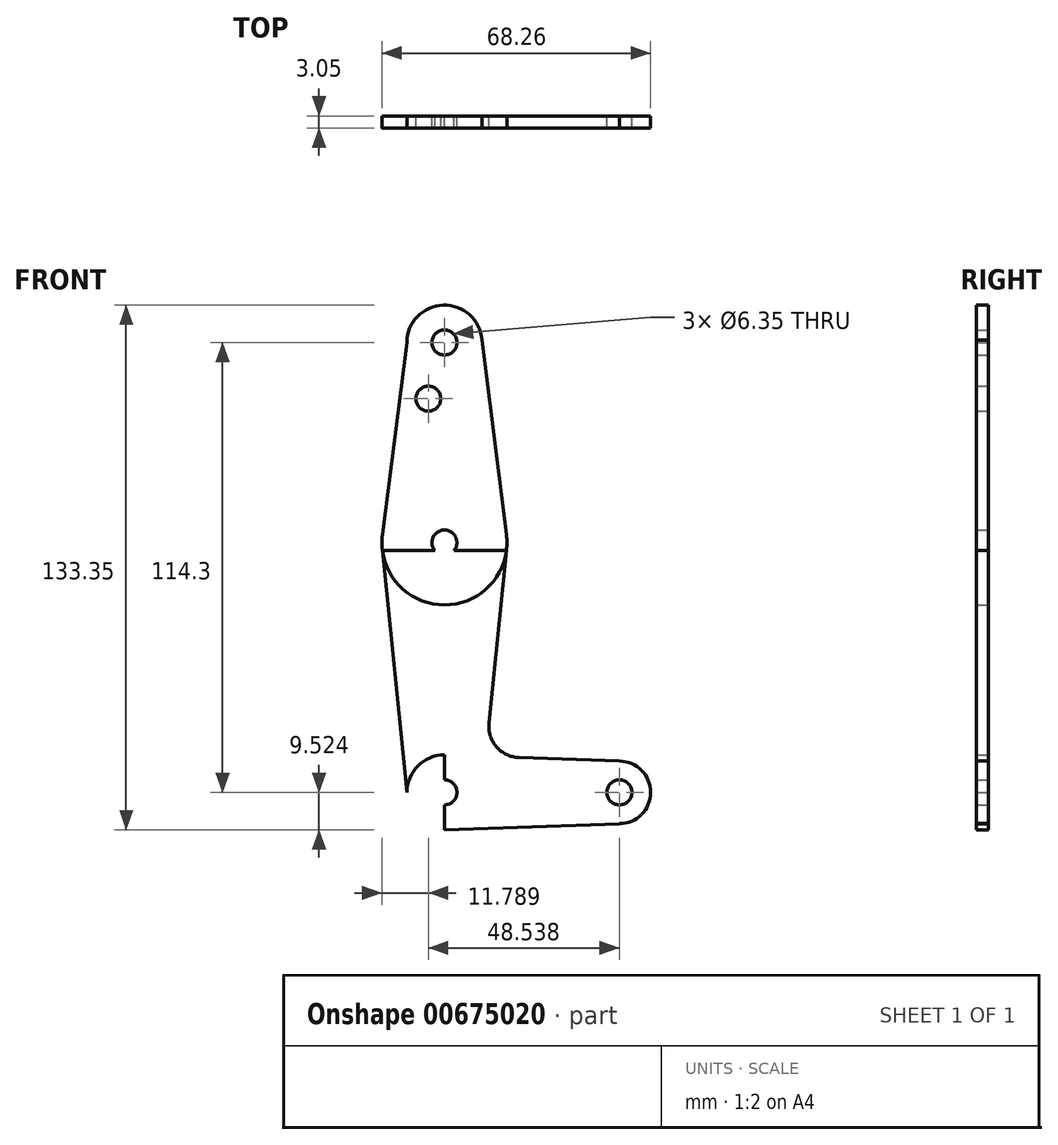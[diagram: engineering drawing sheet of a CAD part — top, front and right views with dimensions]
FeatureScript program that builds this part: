
annotation { "Feature Type Name" : "Feature", "Feature Type Description" : "" }
export const myFeature = defineFeature(function(context is Context, id is Id, definition is map)
    precondition{}
    {
        {
            var Q0;
            Q0=qCreatedBy(makeId("Front.planeOp"),FACE);
            var sketch = newSketch(context, id + "F0", { "sketchPlane" : qUnion([Q0])});
            skLineSegment(sketch, "E0", {"start": v(-73.87, 63.95) * mm, "end": v(-73.87, -50.35) * mm});
            skLineSegment(sketch, "E1", {"start": v(-73.87, -50.35) * mm, "end": v(-29.42, -50.35) * mm});
            skCircle(sketch, "E2", {"center": v(-29.42, -50.35) * mm, "radius": 7.94 * mm});
            skCircle(sketch, "E3", {"center": v(-73.87, 13.15) * mm, "radius": 15.88 * mm});
            skCircle(sketch, "E4", {"center": v(-73.87, 63.95) * mm, "radius": 9.53 * mm});
            skLineSegment(sketch, "E5", {"start": v(-73.87, -50.35) * mm, "end": v(-73.87, 13.15) * mm});
            skCircle(sketch, "E6", {"center": v(-73.87, -50.35) * mm, "radius": 9.53 * mm});
            skLineSegment(sketch, "E7", {"start": v(-64.37, 64.59) * mm, "end": v(-58.12, 15.14) * mm});
            skLineSegment(sketch, "E8", {"start": v(-62.57, -32.75) * mm, "end": v(-58.12, 11.12) * mm});
            skLineSegment(sketch, "E9", {"start": v(-83.4, 63.95) * mm, "end": v(-89.62, 15.14) * mm});
            skLineSegment(sketch, "E10", {"start": v(-83.4, -50.35) * mm, "end": v(-89.62, 11.12) * mm});
            skLineSegment(sketch, "E11", {"start": v(-29.42, -42.4) * mm, "end": v(-54.94, -41.5) * mm});
            skLineSegment(sketch, "E12", {"start": v(-73.87, -59.87) * mm, "end": v(-29.42, -58.29) * mm});
            skCircle(sketch, "E13", {"center": v(-73.87, 63.95) * mm, "radius": 3.18 * mm});
            skCircle(sketch, "E14", {"center": v(-73.87, 13.15) * mm, "radius": 3.18 * mm});
            skCircle(sketch, "E15", {"center": v(-73.87, -50.35) * mm, "radius": 3.18 * mm});
            skCircle(sketch, "E16", {"center": v(-29.42, -50.35) * mm, "radius": 3.18 * mm});
            skPoint(sketch, "E17.newPointB", {"position": v(-73.87, -40.81) * mm});
            skArc(sketch, "E17.filletArc", {"start": v(-62.57, -32.75) * mm, "mid": v(-60.65, -38.77) * mm, "end": v(-54.94, -41.5) * mm});
            skLineSegment(sketch, "E18", {"start": v(-73.87, 49.68) * mm, "end": v(-73.87, 13.15) * mm, "construction": true});
            skCircle(sketch, "E19", {"center": v(-77.96, 49.68) * mm, "radius": 3.18 * mm});
            skLineSegment(sketch, "E20", {"start": v(-89.62, 11.12) * mm, "end": v(-58.12, 11.12) * mm});
            skLineSegment(sketch, "E21", {"start": v(-73.87, -59.87) * mm, "end": v(-73.87, -50.35) * mm});
            skLineSegment(sketch, "E22", {"start": v(-29.42, -42.4) * mm, "end": v(-29.42, -58.29) * mm});
            skSolve(sketch);
        }
        {
            var Q0;
            {var subQ0=sQuery(id+"F0.wireOp",EDGE,"E9");Q0=makeQuery(id+"F0.imprint","IMPRINT",FACE,{"disambiguationData":[TD([[makeQuery(id+"F0.imprint","IMPRINT",EDGE,{"derivedFrom":subQ0}),1.0]])]});}
            var Q1;
            {var subQ5=sQuery(id+"F0.wireOp",EDGE,"E7");Q1=makeQuery(id+"F0.imprint","IMPRINT",FACE,{"disambiguationData":[TD([[makeQuery(id+"F0.imprint","IMPRINT",EDGE,{"derivedFrom":subQ5}),-1.0]])]});}
            var Q2;
            Q2=makeQuery(id+"F0.imprint","IMPRINT",FACE,{"disambiguationData":[TD([[makeQuery(id+"F0.imprint","IMPRINT",EDGE,{"derivedFrom":sQuery(id+"F0.wireOp",EDGE,"E13")}),-1.0]])]});
            var Q3;
            {var subQ1=sQuery(id+"F0.wireOp",EDGE,"E0");var subQ5=sQuery(id+"F0.wireOp",EDGE,"E3");var subQ8=makeQuery(id+"F0.imprint","INTERSECT",VERTEX,{"derivedFrom":[subQ1,subQ5]});Q3=makeQuery(id+"F0.imprint","IMPRINT",FACE,{"disambiguationData":[TD([[makeQuery(id+"F0.imprint","IMPRINT",EDGE,{"disambiguationData":[TD([[subQ8,-1.0]])],"derivedFrom":subQ1}),1.0]])]});}
            var Q4;
            {var subQ1=sQuery(id+"F0.wireOp",EDGE,"E0");var subQ5=sQuery(id+"F0.wireOp",EDGE,"E3");var subQ8=makeQuery(id+"F0.imprint","INTERSECT",VERTEX,{"derivedFrom":[subQ1,subQ5]});Q4=makeQuery(id+"F0.imprint","IMPRINT",FACE,{"disambiguationData":[TD([[makeQuery(id+"F0.imprint","IMPRINT",EDGE,{"disambiguationData":[TD([[subQ8,-1.0]])],"derivedFrom":subQ1}),-1.0]])]});}
            var Q5;
            {var subQ0=sQuery(id+"F0.wireOp",EDGE,"E20");var subQ1=sQuery(id+"F0.wireOp",EDGE,"E3");var subQ2=makeQuery(id+"F0.imprint","INTERSECT",VERTEX,{"disambiguationData":[OD(0.0)],"derivedFrom":[subQ1,subQ0]});Q5=makeQuery(id+"F0.imprint","IMPRINT",FACE,{"disambiguationData":[TD([[makeQuery(id+"F0.imprint","IMPRINT",EDGE,{"disambiguationData":[TD([[subQ2,-1.0]])],"derivedFrom":subQ1}),1.0]])]});}
            var Q6;
            {var subQ0=sQuery(id+"F0.wireOp",EDGE,"E20");var subQ1=sQuery(id+"F0.wireOp",EDGE,"E3");var subQ2=makeQuery(id+"F0.imprint","INTERSECT",VERTEX,{"disambiguationData":[OD(1.0)],"derivedFrom":[subQ1,subQ0]});Q6=makeQuery(id+"F0.imprint","IMPRINT",FACE,{"disambiguationData":[TD([[makeQuery(id+"F0.imprint","IMPRINT",EDGE,{"disambiguationData":[TD([[subQ2,1.0]])],"derivedFrom":subQ1}),1.0]])]});}
            var Q7;
            {var subQ12=sQuery(id+"F0.wireOp",EDGE,"E8");Q7=makeQuery(id+"F0.imprint","IMPRINT",FACE,{"disambiguationData":[TD([[makeQuery(id+"F0.imprint","IMPRINT",EDGE,{"derivedFrom":subQ12}),1.0]])]});}
            var Q8;
            {var subQ0=sQuery(id+"F0.wireOp",EDGE,"E10");Q8=makeQuery(id+"F0.imprint","IMPRINT",FACE,{"disambiguationData":[TD([[makeQuery(id+"F0.imprint","IMPRINT",EDGE,{"derivedFrom":subQ0}),-1.0]])]});}
            var Q9;
            {var subQ0=sQuery(id+"F0.wireOp",EDGE,"E15");var subQ1=sQuery(id+"F0.wireOp",EDGE,"E5");var subQ2=makeQuery(id+"F0.imprint","INTERSECT",VERTEX,{"derivedFrom":[subQ1,subQ0]});Q9=makeQuery(id+"F0.imprint","IMPRINT",FACE,{"disambiguationData":[TD([[makeQuery(id+"F0.imprint","IMPRINT",EDGE,{"disambiguationData":[TD([[subQ2,-1.0]])],"derivedFrom":subQ1}),1.0]])]});}
            var Q10;
            {var subQ0=sQuery(id+"F0.wireOp",EDGE,"E15");var subQ1=sQuery(id+"F0.wireOp",EDGE,"E1");var subQ2=makeQuery(id+"F0.imprint","INTERSECT",VERTEX,{"derivedFrom":[subQ1,subQ0]});Q10=makeQuery(id+"F0.imprint","IMPRINT",FACE,{"disambiguationData":[TD([[makeQuery(id+"F0.imprint","IMPRINT",EDGE,{"disambiguationData":[TD([[subQ2,-1.0]])],"derivedFrom":subQ1}),1.0]])]});}
            var Q11;
            {var subQ5=sQuery(id+"F0.wireOp",EDGE,"E15");var subQ6=sQuery(id+"F0.wireOp",EDGE,"E1");var subQ7=makeQuery(id+"F0.imprint","INTERSECT",VERTEX,{"derivedFrom":[subQ6,subQ5]});Q11=makeQuery(id+"F0.imprint","IMPRINT",FACE,{"disambiguationData":[TD([[makeQuery(id+"F0.imprint","IMPRINT",EDGE,{"disambiguationData":[TD([[subQ7,-1.0]])],"derivedFrom":subQ6}),-1.0]])]});}
            var Q12;
            {var subQ3=sQuery(id+"F0.wireOp",EDGE,"E6");var subQ7=sQuery(id+"F0.wireOp",EDGE,"E1");var subQ9=makeQuery(id+"F0.imprint","INTERSECT",VERTEX,{"derivedFrom":[subQ7,subQ3]});Q12=makeQuery(id+"F0.imprint","IMPRINT",FACE,{"disambiguationData":[TD([[makeQuery(id+"F0.imprint","IMPRINT",EDGE,{"disambiguationData":[TD([[subQ9,-1.0]])],"derivedFrom":subQ7}),-1.0]])]});}
            var Q13;
            {var subQ0=sQuery(id+"F0.wireOp",EDGE,"E2");var subQ1=sQuery(id+"F0.wireOp",EDGE,"E1");var subQ2=makeQuery(id+"F0.imprint","INTERSECT",VERTEX,{"derivedFrom":[subQ1,subQ0]});Q13=makeQuery(id+"F0.imprint","IMPRINT",FACE,{"disambiguationData":[TD([[makeQuery(id+"F0.imprint","IMPRINT",EDGE,{"disambiguationData":[TD([[subQ2,-1.0]])],"derivedFrom":subQ1}),1.0]])]});}
            var Q14;
            {var subQ0=sQuery(id+"F0.wireOp",EDGE,"E22");var subQ4=sQuery(id+"F0.wireOp",EDGE,"E16");var subQ5=makeQuery(id+"F0.imprint","INTERSECT",VERTEX,{"disambiguationData":[OD(0.0)],"derivedFrom":[subQ4,subQ0]});Q14=makeQuery(id+"F0.imprint","IMPRINT",FACE,{"disambiguationData":[TD([[makeQuery(id+"F0.imprint","IMPRINT",EDGE,{"disambiguationData":[TD([[subQ5,1.0]])],"derivedFrom":subQ4}),-1.0]])]});}
            var Q15;
            {var subQ0=sQuery(id+"F0.wireOp",EDGE,"E2");var subQ1=sQuery(id+"F0.wireOp",EDGE,"E1");var subQ2=makeQuery(id+"F0.imprint","INTERSECT",VERTEX,{"derivedFrom":[subQ1,subQ0]});Q15=makeQuery(id+"F0.imprint","IMPRINT",FACE,{"disambiguationData":[TD([[makeQuery(id+"F0.imprint","IMPRINT",EDGE,{"disambiguationData":[TD([[subQ2,-1.0]])],"derivedFrom":subQ1}),-1.0]])]});}
            extrude(context, id + "F1", {"entities" : qUnion([Q0, Q1, Q2, Q3, Q4, Q5, Q6, Q7, Q8, Q9, Q10, Q11, Q12, Q13, Q14, Q15]), "depth" : 3.05 * mm, "offsetDistance" : 25.4 * mm});
        }
    });
